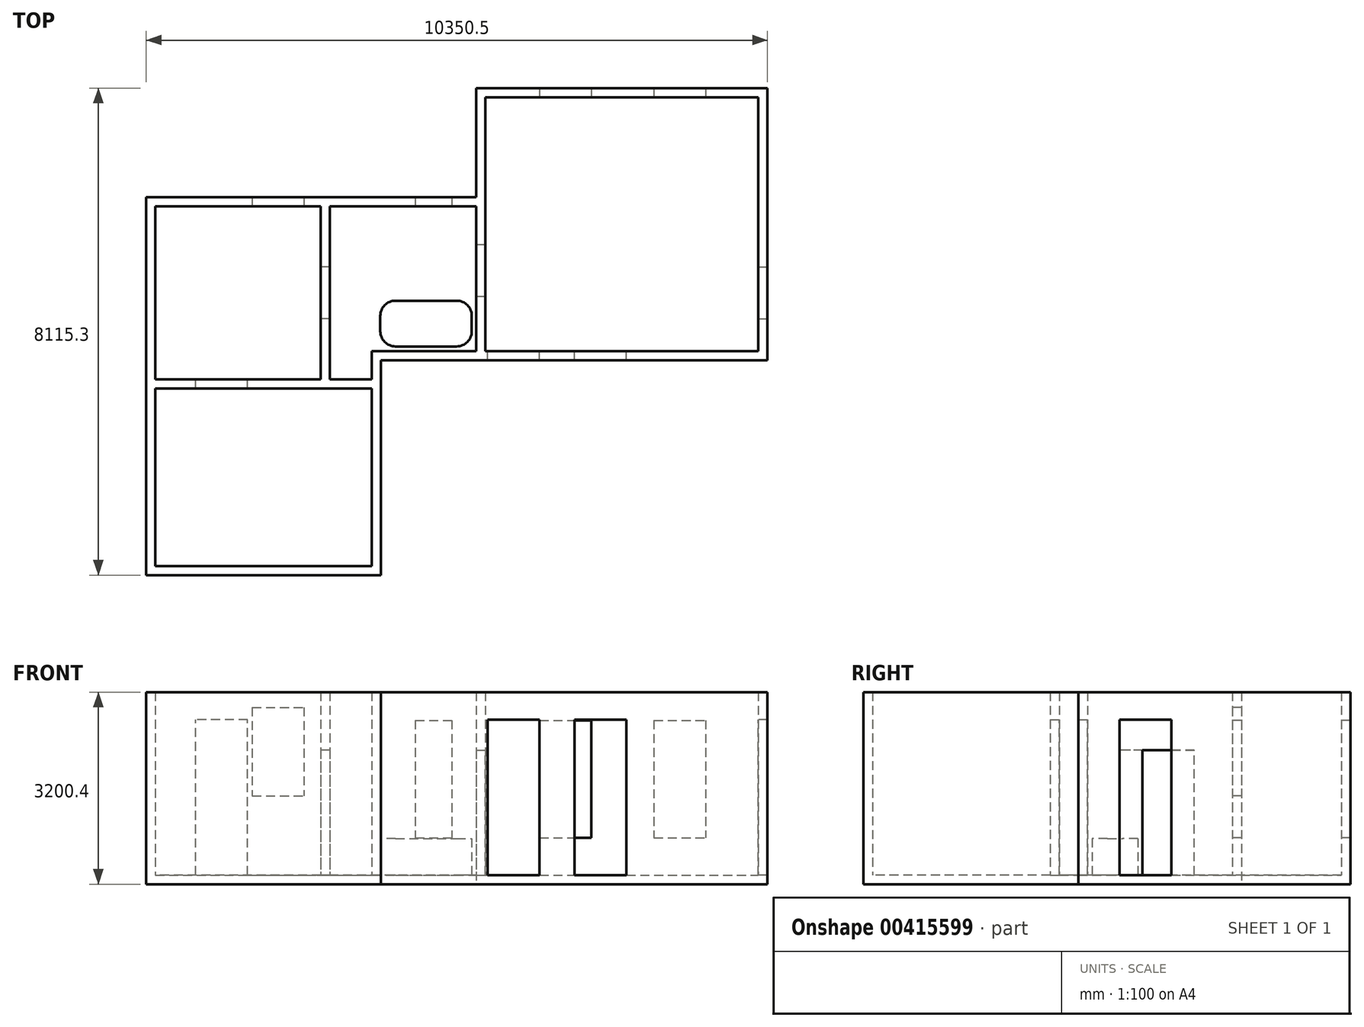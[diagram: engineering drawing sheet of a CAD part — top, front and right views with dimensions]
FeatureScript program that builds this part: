
annotation { "Feature Type Name" : "Feature", "Feature Type Description" : "" }
export const myFeature = defineFeature(function(context is Context, id is Id, definition is map)
    precondition{}
    {
        {
            var Q0;
            Q0=qCreatedBy(makeId("Top.planeOp"),FACE);
            var sketch = newSketch(context, id + "F0", { "sketchPlane" : qUnion([Q0])});
            skLineSegment(sketch, "E0", {"start": v(0, 0) * mm, "end": v(-4546.6, 0) * mm});
            skLineSegment(sketch, "E1", {"start": v(-10045.7, -1816.1) * mm, "end": v(-10045.7, -7810.5) * mm});
            skLineSegment(sketch, "E2", {"start": v(-10045.7, -7810.5) * mm, "end": v(-6438.9, -7810.5) * mm});
            skLineSegment(sketch, "E3", {"start": v(-6438.9, -7810.5) * mm, "end": v(-6438.9, -4229.1) * mm});
            skLineSegment(sketch, "E4", {"start": v(-6438.9, -4229.1) * mm, "end": v(0, -4229.1) * mm});
            skLineSegment(sketch, "E5", {"start": v(0, -4229.1) * mm, "end": v(0, 0) * mm});
            skLineSegment(sketch, "E6", {"start": v(-4546.6, 0) * mm, "end": v(-4546.6, -1816.1) * mm});
            skLineSegment(sketch, "E7", {"start": v(-4546.6, -1816.1) * mm, "end": v(-10045.7, -1816.1) * mm});
            skLineSegment(sketch, "E8.0", {"start": v(-4699, 152.4) * mm, "end": v(-4699, -1663.7) * mm});
            skLineSegment(sketch, "E8.1", {"start": v(152.4, 152.4) * mm, "end": v(-4699, 152.4) * mm});
            skLineSegment(sketch, "E8.2", {"start": v(-4699, -1663.7) * mm, "end": v(-10198.1, -1663.7) * mm});
            skLineSegment(sketch, "E8.3", {"start": v(152.4, -4381.5) * mm, "end": v(152.4, 152.4) * mm});
            skLineSegment(sketch, "E8.4", {"start": v(-10198.1, -1663.7) * mm, "end": v(-10198.1, -7962.9) * mm});
            skLineSegment(sketch, "E8.5", {"start": v(-10198.1, -7962.9) * mm, "end": v(-6286.5, -7962.9) * mm});
            skLineSegment(sketch, "E8.6", {"start": v(-6286.5, -7962.9) * mm, "end": v(-6286.5, -4381.5) * mm});
            skLineSegment(sketch, "E8.7", {"start": v(-6286.5, -4381.5) * mm, "end": v(152.4, -4381.5) * mm});
            skSolve(sketch);
        }
        {
            var Q0;
            Q0 = qSketchRegion(id + "F0", true);
            extrude(context, id + "F1", {"entities" : qUnion([Q0]), "depth" : 3048 * mm});
        }
        {
            var Q0;
            Q0=makeQuery(id+"F1.opExtrude","CAP_FACE",FACE,{"disambiguationData":[OSD([sQuery(id+"F0.wireOp",EDGE,"E0"),sQuery(id+"F0.wireOp",EDGE,"E1"),sQuery(id+"F0.wireOp",EDGE,"E2"),sQuery(id+"F0.wireOp",EDGE,"E3"),sQuery(id+"F0.wireOp",EDGE,"E4"),sQuery(id+"F0.wireOp",EDGE,"E5"),sQuery(id+"F0.wireOp",EDGE,"E6"),sQuery(id+"F0.wireOp",EDGE,"E7"),sQuery(id+"F0.wireOp",EDGE,"E8.0"),sQuery(id+"F0.wireOp",EDGE,"E8.1"),sQuery(id+"F0.wireOp",EDGE,"E8.2"),sQuery(id+"F0.wireOp",EDGE,"E8.3"),sQuery(id+"F0.wireOp",EDGE,"E8.4"),sQuery(id+"F0.wireOp",EDGE,"E8.5"),sQuery(id+"F0.wireOp",EDGE,"E8.6"),sQuery(id+"F0.wireOp",EDGE,"E8.7")])],"isStart":true});
            var sketch = newSketch(context, id + "F2", { "sketchPlane" : qUnion([Q0])});
            skLineSegment(sketch, "E9", {"start": v(-10198.1, 7962.9) * mm, "end": v(-6286.5, 7962.9) * mm});
            skLineSegment(sketch, "E10", {"start": v(-6286.5, 7962.9) * mm, "end": v(-6286.5, 4381.5) * mm});
            skLineSegment(sketch, "E11", {"start": v(-6286.5, 4381.5) * mm, "end": v(152.4, 4381.5) * mm});
            skLineSegment(sketch, "E12", {"start": v(152.4, 4381.5) * mm, "end": v(152.4, -152.4) * mm});
            skLineSegment(sketch, "E13", {"start": v(152.4, -152.4) * mm, "end": v(-4699, -152.4) * mm});
            skLineSegment(sketch, "E14", {"start": v(-4699, -152.4) * mm, "end": v(-4699, 1663.7) * mm});
            skLineSegment(sketch, "E15", {"start": v(-4699, 1663.7) * mm, "end": v(-10198.1, 1663.7) * mm});
            skLineSegment(sketch, "E16", {"start": v(-10198.1, 1663.7) * mm, "end": v(-10198.1, 7962.9) * mm});
            skSolve(sketch);
        }
        {
            var Q0;
            Q0 = qSketchRegion(id + "F2", true);
            extrude(context, id + "F3", {"entities" : qUnion([Q0]), "operationType" : NewBodyOperationType.ADD, "depth" : 152.4 * mm});
        }
        {
            var Q0;
            Q0=makeQuery(id+"F1.opExtrude","SWEPT_FACE",FACE,{"disambiguationData":[OSD([sQuery(id+"F0.wireOp",EDGE,"E4")])]});
            var sketch = newSketch(context, id + "F4", { "sketchPlane" : qUnion([Q0])});
            skLineSegment(sketch, "E17.bottom", {"start": v(2197.1, 0) * mm, "end": v(3060.7, 0) * mm});
            skLineSegment(sketch, "E17.top", {"start": v(2197.1, 2590.8) * mm, "end": v(3060.7, 2590.8) * mm});
            skLineSegment(sketch, "E17.left", {"start": v(2197.1, 0) * mm, "end": v(2197.1, 2590.8) * mm});
            skLineSegment(sketch, "E17.right", {"start": v(3060.7, 0) * mm, "end": v(3060.7, 2590.8) * mm});
            skLineSegment(sketch, "E18.bottom", {"start": v(3644.9, 0) * mm, "end": v(4508.5, 0) * mm});
            skLineSegment(sketch, "E18.top", {"start": v(3644.9, 2590.8) * mm, "end": v(4508.5, 2590.8) * mm});
            skLineSegment(sketch, "E18.left", {"start": v(3644.9, 0) * mm, "end": v(3644.9, 2590.8) * mm});
            skLineSegment(sketch, "E18.right", {"start": v(4508.5, 0) * mm, "end": v(4508.5, 2590.8) * mm});
            skSolve(sketch);
        }
        {
            var Q0;
            Q0 = qSketchRegion(id + "F4", true);
            extrude(context, id + "F5", {"entities" : qUnion([Q0]), "operationType" : NewBodyOperationType.REMOVE, "endBound" : BoundingType.THROUGH_ALL, "oppositeDirection" : true, "depth" : 25.4 * mm});
        }
        {
            var Q0;
            Q0=makeQuery(id+"F1.opExtrude","SWEPT_FACE",FACE,{"disambiguationData":[OSD([sQuery(id+"F0.wireOp",EDGE,"E0")])]});
            var sketch = newSketch(context, id + "F6", { "sketchPlane" : qUnion([Q0])});
            skLineSegment(sketch, "E19.bottom", {"start": v(-3644.9, 2578.1) * mm, "end": v(-2781.3, 2578.1) * mm});
            skLineSegment(sketch, "E19.top", {"start": v(-3644.9, 622.3) * mm, "end": v(-2781.3, 622.3) * mm});
            skLineSegment(sketch, "E19.left", {"start": v(-3644.9, 2578.1) * mm, "end": v(-3644.9, 622.3) * mm});
            skLineSegment(sketch, "E19.right", {"start": v(-2781.3, 2578.1) * mm, "end": v(-2781.3, 622.3) * mm});
            skLineSegment(sketch, "E20.bottom", {"start": v(-1739.9, 2578.1) * mm, "end": v(-876.3, 2578.1) * mm});
            skLineSegment(sketch, "E20.top", {"start": v(-1739.9, 622.3) * mm, "end": v(-876.3, 622.3) * mm});
            skLineSegment(sketch, "E20.left", {"start": v(-1739.9, 2578.1) * mm, "end": v(-1739.9, 622.3) * mm});
            skLineSegment(sketch, "E20.right", {"start": v(-876.3, 2578.1) * mm, "end": v(-876.3, 622.3) * mm});
            skSolve(sketch);
        }
        {
            var Q0;
            Q0 = qSketchRegion(id + "F6", true);
            extrude(context, id + "F7", {"entities" : qUnion([Q0]), "operationType" : NewBodyOperationType.REMOVE, "endBound" : BoundingType.THROUGH_ALL, "oppositeDirection" : true, "depth" : 25.4 * mm});
        }
        {
            var Q0;
            Q0=makeQuery(id+"F1.opExtrude","SWEPT_FACE",FACE,{"disambiguationData":[OSD([sQuery(id+"F0.wireOp",EDGE,"E5")])]});
            var sketch = newSketch(context, id + "F8", { "sketchPlane" : qUnion([Q0])});
            skLineSegment(sketch, "E21.bottom", {"start": v(3695.7, 0) * mm, "end": v(2832.1, 0) * mm});
            skLineSegment(sketch, "E21.top", {"start": v(3695.7, 2590.8) * mm, "end": v(2832.1, 2590.8) * mm});
            skLineSegment(sketch, "E21.left", {"start": v(3695.7, 0) * mm, "end": v(3695.7, 2590.8) * mm});
            skLineSegment(sketch, "E21.right", {"start": v(2832.1, 0) * mm, "end": v(2832.1, 2590.8) * mm});
            skSolve(sketch);
        }
        {
            var Q0;
            Q0 = qSketchRegion(id + "F8", true);
            extrude(context, id + "F9", {"entities" : qUnion([Q0]), "operationType" : NewBodyOperationType.REMOVE, "endBound" : BoundingType.THROUGH_ALL, "oppositeDirection" : true, "depth" : 25.4 * mm});
        }
        {
            var Q0;
            Q0=makeQuery(id+"F9.boolean.opBoolean","MERGE",FACE,{"derivedFrom":[makeQuery(id+"F5.boolean.opBoolean","MERGE",FACE,{"derivedFrom":[makeQuery(id+"F3.opExtrude","CAP_FACE",FACE,{"disambiguationData":[OSD([sQuery(id+"F2.wireOp",EDGE,"E9"),sQuery(id+"F2.wireOp",EDGE,"E10"),sQuery(id+"F2.wireOp",EDGE,"E11"),sQuery(id+"F2.wireOp",EDGE,"E12"),sQuery(id+"F2.wireOp",EDGE,"E13"),sQuery(id+"F2.wireOp",EDGE,"E14"),sQuery(id+"F2.wireOp",EDGE,"E15"),sQuery(id+"F2.wireOp",EDGE,"E16")])],"isStart":true}),makeQuery(id+"F5.opExtrude","SWEPT_FACE",FACE,{"disambiguationData":[OSD([sQuery(id+"F4.wireOp",EDGE,"E17.bottom")])]}),makeQuery(id+"F5.opExtrude","SWEPT_FACE",FACE,{"disambiguationData":[OSD([sQuery(id+"F4.wireOp",EDGE,"E18.bottom")])]})]}),makeQuery(id+"F9.opExtrude","SWEPT_FACE",FACE,{"disambiguationData":[OSD([sQuery(id+"F8.wireOp",EDGE,"E21.bottom")])]})]});
            var sketch = newSketch(context, id + "F10", { "sketchPlane" : qUnion([Q0])});
            skLineSegment(sketch, "E22.bottom", {"start": v(-4546.6, -1816.1) * mm, "end": v(-4699, -1816.1) * mm});
            skLineSegment(sketch, "E22.top", {"start": v(-4546.6, -4229.1) * mm, "end": v(-4699, -4229.1) * mm});
            skLineSegment(sketch, "E22.left", {"start": v(-4546.6, -1816.1) * mm, "end": v(-4546.6, -4229.1) * mm});
            skLineSegment(sketch, "E22.right", {"start": v(-4699, -1816.1) * mm, "end": v(-4699, -4229.1) * mm});
            skLineSegment(sketch, "E23.bottom", {"start": v(-10045.7, -4699) * mm, "end": v(-6438.9, -4699) * mm});
            skLineSegment(sketch, "E23.top", {"start": v(-10045.7, -4851.4) * mm, "end": v(-6438.9, -4851.4) * mm});
            skLineSegment(sketch, "E23.left", {"start": v(-10045.7, -4699) * mm, "end": v(-10045.7, -4851.4) * mm});
            skLineSegment(sketch, "E23.right", {"start": v(-6438.9, -4699) * mm, "end": v(-6438.9, -4851.4) * mm});
            skSolve(sketch);
        }
        {
            var Q0;
            Q0 = qSketchRegion(id + "F10", true);
            var Q1;
            Q1=makeQuery(id+"F1.opExtrude","CAP_FACE",FACE,{"disambiguationData":[OSD([sQuery(id+"F0.wireOp",EDGE,"E0"),sQuery(id+"F0.wireOp",EDGE,"E1"),sQuery(id+"F0.wireOp",EDGE,"E2"),sQuery(id+"F0.wireOp",EDGE,"E3"),sQuery(id+"F0.wireOp",EDGE,"E4"),sQuery(id+"F0.wireOp",EDGE,"E5"),sQuery(id+"F0.wireOp",EDGE,"E6"),sQuery(id+"F0.wireOp",EDGE,"E7"),sQuery(id+"F0.wireOp",EDGE,"E8.0"),sQuery(id+"F0.wireOp",EDGE,"E8.1"),sQuery(id+"F0.wireOp",EDGE,"E8.2"),sQuery(id+"F0.wireOp",EDGE,"E8.3"),sQuery(id+"F0.wireOp",EDGE,"E8.4"),sQuery(id+"F0.wireOp",EDGE,"E8.5"),sQuery(id+"F0.wireOp",EDGE,"E8.6"),sQuery(id+"F0.wireOp",EDGE,"E8.7")])],"isStart":false});
            extrude(context, id + "F11", {"entities" : qUnion([Q0]), "operationType" : NewBodyOperationType.ADD, "endBound" : BoundingType.UP_TO_SURFACE, "endBoundEntityFace" : qUnion([Q1]), "depth" : 25.4 * mm});
        }
        {
            var Q0;
            Q0=makeQuery(id+"F1.opExtrude","SWEPT_FACE",FACE,{"disambiguationData":[OSD([sQuery(id+"F0.wireOp",EDGE,"E7")])]});
            var sketch = newSketch(context, id + "F12", { "sketchPlane" : qUnion([Q0])});
            skLineSegment(sketch, "E24.bottom", {"start": v(-5715, 2578.1) * mm, "end": v(-5105.4, 2578.1) * mm});
            skLineSegment(sketch, "E24.top", {"start": v(-5715, 622.3) * mm, "end": v(-5105.4, 622.3) * mm});
            skLineSegment(sketch, "E24.left", {"start": v(-5715, 2578.1) * mm, "end": v(-5715, 622.3) * mm});
            skLineSegment(sketch, "E24.right", {"start": v(-5105.4, 2578.1) * mm, "end": v(-5105.4, 622.3) * mm});
            skLineSegment(sketch, "E25.bottom", {"start": v(-8432.8, 2794) * mm, "end": v(-7569.2, 2794) * mm});
            skLineSegment(sketch, "E25.top", {"start": v(-8432.8, 1320.8) * mm, "end": v(-7569.2, 1320.8) * mm});
            skLineSegment(sketch, "E25.left", {"start": v(-8432.8, 2794) * mm, "end": v(-8432.8, 1320.8) * mm});
            skLineSegment(sketch, "E25.right", {"start": v(-7569.2, 2794) * mm, "end": v(-7569.2, 1320.8) * mm});
            skSolve(sketch);
        }
        {
            var Q0;
            Q0 = qSketchRegion(id + "F12", true);
            extrude(context, id + "F13", {"entities" : qUnion([Q0]), "operationType" : NewBodyOperationType.REMOVE, "endBound" : BoundingType.THROUGH_ALL, "oppositeDirection" : true, "depth" : 25.4 * mm});
        }
        {
            var Q0;
            Q0=makeQuery(id+"F11.boolean.opBoolean","SPLIT",FACE,{"disambiguationData":[TD([makeQuery(id+"F1.opExtrude","SWEPT_FACE",FACE,{"disambiguationData":[OSD([sQuery(id+"F0.wireOp",EDGE,"E7")])]})])],"derivedFrom":makeQuery(id+"F9.boolean.opBoolean","MERGE",FACE,{"derivedFrom":[makeQuery(id+"F5.boolean.opBoolean","MERGE",FACE,{"derivedFrom":[makeQuery(id+"F3.opExtrude","CAP_FACE",FACE,{"disambiguationData":[OSD([sQuery(id+"F2.wireOp",EDGE,"E9"),sQuery(id+"F2.wireOp",EDGE,"E10"),sQuery(id+"F2.wireOp",EDGE,"E11"),sQuery(id+"F2.wireOp",EDGE,"E12"),sQuery(id+"F2.wireOp",EDGE,"E13"),sQuery(id+"F2.wireOp",EDGE,"E14"),sQuery(id+"F2.wireOp",EDGE,"E15"),sQuery(id+"F2.wireOp",EDGE,"E16")])],"isStart":true}),makeQuery(id+"F5.opExtrude","SWEPT_FACE",FACE,{"disambiguationData":[OSD([sQuery(id+"F4.wireOp",EDGE,"E17.bottom")])]}),makeQuery(id+"F5.opExtrude","SWEPT_FACE",FACE,{"disambiguationData":[OSD([sQuery(id+"F4.wireOp",EDGE,"E18.bottom")])]})]}),makeQuery(id+"F9.opExtrude","SWEPT_FACE",FACE,{"disambiguationData":[OSD([sQuery(id+"F8.wireOp",EDGE,"E21.bottom")])]})]})});
            var sketch = newSketch(context, id + "F14", { "sketchPlane" : qUnion([Q0])});
            skLineSegment(sketch, "E26.bottom", {"start": v(-7289.8, -1816.1) * mm, "end": v(-7137.4, -1816.1) * mm});
            skLineSegment(sketch, "E26.top", {"start": v(-7289.8, -4699) * mm, "end": v(-7137.4, -4699) * mm});
            skLineSegment(sketch, "E26.left", {"start": v(-7289.8, -1816.1) * mm, "end": v(-7289.8, -4699) * mm});
            skLineSegment(sketch, "E26.right", {"start": v(-7137.4, -1816.1) * mm, "end": v(-7137.4, -4699) * mm});
            skSolve(sketch);
        }
        {
            var Q0;
            Q0 = qSketchRegion(id + "F14", true);
            var Q1;
            {var subQ0=sQuery(id+"F0.wireOp",EDGE,"E8.7");var subQ1=sQuery(id+"F0.wireOp",EDGE,"E8.6");var subQ2=sQuery(id+"F0.wireOp",EDGE,"E8.5");var subQ3=sQuery(id+"F0.wireOp",EDGE,"E8.4");var subQ4=sQuery(id+"F0.wireOp",EDGE,"E8.3");var subQ5=sQuery(id+"F0.wireOp",EDGE,"E8.2");var subQ6=sQuery(id+"F0.wireOp",EDGE,"E8.1");var subQ7=sQuery(id+"F0.wireOp",EDGE,"E8.0");var subQ8=sQuery(id+"F0.wireOp",EDGE,"E7");var subQ9=sQuery(id+"F0.wireOp",EDGE,"E6");var subQ10=sQuery(id+"F0.wireOp",EDGE,"E5");var subQ11=sQuery(id+"F0.wireOp",EDGE,"E4");var subQ12=sQuery(id+"F0.wireOp",EDGE,"E3");var subQ13=sQuery(id+"F0.wireOp",EDGE,"E2");var subQ14=sQuery(id+"F0.wireOp",EDGE,"E1");var subQ15=sQuery(id+"F0.wireOp",EDGE,"E0");Q1=makeQuery(id+"F11.boolean.opBoolean","MERGE",FACE,{"derivedFrom":[makeQuery(id+"F1.opExtrude","CAP_FACE",FACE,{"disambiguationData":[OSD([subQ15,subQ14,subQ13,subQ12,subQ11,subQ10,subQ9,subQ8,subQ7,subQ6,subQ5,subQ4,subQ3,subQ2,subQ1,subQ0])],"isStart":false}),makeQuery(id+"F11.opExtrude","CAP_FACE",FACE,{"disambiguationData":[OSD([subQ15,subQ14,subQ13,subQ12,subQ11,subQ10,subQ9,subQ8,subQ7,subQ6,subQ5,subQ4,subQ3,subQ2,subQ1,subQ0]),ownerDisambiguation([makeQuery(id+"F10.imprint","IMPRINT",EDGE,{"derivedFrom":sQuery(id+"F10.wireOp",EDGE,"E22.bottom")})])],"isStart":false}),makeQuery(id+"F11.opExtrude","CAP_FACE",FACE,{"disambiguationData":[OSD([subQ15,subQ14,subQ13,subQ12,subQ11,subQ10,subQ9,subQ8,subQ7,subQ6,subQ5,subQ4,subQ3,subQ2,subQ1,subQ0]),ownerDisambiguation([makeQuery(id+"F10.imprint","IMPRINT",EDGE,{"derivedFrom":sQuery(id+"F10.wireOp",EDGE,"E23.bottom")})])],"isStart":false})]});}
            extrude(context, id + "F15", {"entities" : qUnion([Q0]), "operationType" : NewBodyOperationType.ADD, "endBound" : BoundingType.UP_TO_SURFACE, "endBoundEntityFace" : qUnion([Q1]), "depth" : 25.4 * mm});
        }
        {
            var Q0;
            Q0=makeQuery(id+"F11.boolean.opBoolean","MERGE",FACE,{"derivedFrom":[makeQuery(id+"F1.opExtrude","SWEPT_FACE",FACE,{"disambiguationData":[OSD([sQuery(id+"F0.wireOp",EDGE,"E6")])]}),makeQuery(id+"F11.opExtrude","SWEPT_FACE",FACE,{"disambiguationData":[OSD([sQuery(id+"F10.wireOp",EDGE,"E22.left")])]})]});
            var sketch = newSketch(context, id + "F16", { "sketchPlane" : qUnion([Q0])});
            skLineSegment(sketch, "E27.bottom", {"start": v(-3314.7, 0) * mm, "end": v(-2451.1, 0) * mm});
            skLineSegment(sketch, "E27.top", {"start": v(-3314.7, 2082.8) * mm, "end": v(-2451.1, 2082.8) * mm});
            skLineSegment(sketch, "E27.left", {"start": v(-3314.7, 0) * mm, "end": v(-3314.7, 2082.8) * mm});
            skLineSegment(sketch, "E27.right", {"start": v(-2451.1, 0) * mm, "end": v(-2451.1, 2082.8) * mm});
            skSolve(sketch);
        }
        {
            var Q0;
            Q0 = qSketchRegion(id + "F16", true);
            var Q1;
            Q1=makeQuery(id+"F11.opExtrude","SWEPT_FACE",FACE,{"disambiguationData":[OSD([sQuery(id+"F10.wireOp",EDGE,"E22.right")])]});
            extrude(context, id + "F17", {"entities" : qUnion([Q0]), "operationType" : NewBodyOperationType.REMOVE, "endBound" : BoundingType.UP_TO_SURFACE, "oppositeDirection" : true, "endBoundEntityFace" : qUnion([Q1]), "depth" : 25.4 * mm});
        }
        {
            var Q0;
            {var subQ14=sQuery(id+"F0.wireOp",EDGE,"E1");var subQ16=sQuery(id+"F10.wireOp",EDGE,"E23.bottom");Q0=makeQuery(id+"F15.boolean.opBoolean","SPLIT",FACE,{"disambiguationData":[TD([makeQuery(id+"F1.opExtrude","SWEPT_FACE",FACE,{"disambiguationData":[OSD([subQ14])]})])],"derivedFrom":makeQuery(id+"F11.opExtrude","SWEPT_FACE",FACE,{"disambiguationData":[OSD([subQ16])]})});}
            var sketch = newSketch(context, id + "F18", { "sketchPlane" : qUnion([Q0])});
            skLineSegment(sketch, "E28.bottom", {"start": v(8509, 0) * mm, "end": v(9372.6, 0) * mm});
            skLineSegment(sketch, "E28.top", {"start": v(8509, 2590.8) * mm, "end": v(9372.6, 2590.8) * mm});
            skLineSegment(sketch, "E28.left", {"start": v(8509, 0) * mm, "end": v(8509, 2590.8) * mm});
            skLineSegment(sketch, "E28.right", {"start": v(9372.6, 0) * mm, "end": v(9372.6, 2590.8) * mm});
            skSolve(sketch);
        }
        {
            var Q0;
            Q0 = qSketchRegion(id + "F18", true);
            var Q1;
            Q1=makeQuery(id+"F11.opExtrude","SWEPT_FACE",FACE,{"disambiguationData":[OSD([sQuery(id+"F10.wireOp",EDGE,"E23.top")])]});
            extrude(context, id + "F19", {"entities" : qUnion([Q0]), "operationType" : NewBodyOperationType.REMOVE, "endBound" : BoundingType.UP_TO_SURFACE, "oppositeDirection" : true, "endBoundEntityFace" : qUnion([Q1]), "depth" : 25.4 * mm});
        }
        {
            var Q0;
            Q0=makeQuery(id+"F15.opExtrude","SWEPT_FACE",FACE,{"disambiguationData":[OSD([sQuery(id+"F14.wireOp",EDGE,"E26.left")])]});
            var sketch = newSketch(context, id + "F20", { "sketchPlane" : qUnion([Q0])});
            skLineSegment(sketch, "E29.bottom", {"start": v(2825.75, 2082.8) * mm, "end": v(3689.35, 2082.8) * mm});
            skLineSegment(sketch, "E29.top", {"start": v(2825.75, 0) * mm, "end": v(3689.35, 0) * mm});
            skLineSegment(sketch, "E29.left", {"start": v(2825.75, 2082.8) * mm, "end": v(2825.75, 0) * mm});
            skLineSegment(sketch, "E29.right", {"start": v(3689.35, 2082.8) * mm, "end": v(3689.35, 0) * mm});
            skSolve(sketch);
        }
        {
            var Q0;
            Q0 = qSketchRegion(id + "F20", true);
            var Q1;
            Q1=makeQuery(id+"F15.opExtrude","SWEPT_FACE",FACE,{"disambiguationData":[OSD([sQuery(id+"F14.wireOp",EDGE,"E26.right")])]});
            extrude(context, id + "F21", {"entities" : qUnion([Q0]), "operationType" : NewBodyOperationType.REMOVE, "endBound" : BoundingType.UP_TO_SURFACE, "oppositeDirection" : true, "endBoundEntityFace" : qUnion([Q1]), "depth" : 25.4 * mm});
        }
        {
            var Q0;
            {var subQ0=makeQuery(id+"F1.opExtrude","SWEPT_FACE",FACE,{"disambiguationData":[OSD([sQuery(id+"F0.wireOp",EDGE,"E1")])]});var subQ1=makeQuery(id+"F1.opExtrude","SWEPT_FACE",FACE,{"disambiguationData":[OSD([sQuery(id+"F0.wireOp",EDGE,"E7")])]});var subQ4=makeQuery(id+"F1.opExtrude","SWEPT_FACE",FACE,{"disambiguationData":[OSD([sQuery(id+"F0.wireOp",EDGE,"E3")])]});var subQ6=sQuery(id+"F2.wireOp",EDGE,"E12");var subQ7=sQuery(id+"F2.wireOp",EDGE,"E11");var subQ8=makeQuery(id+"F9.boolean.opBoolean","MERGE",FACE,{"derivedFrom":[makeQuery(id+"F5.boolean.opBoolean","MERGE",FACE,{"derivedFrom":[makeQuery(id+"F3.opExtrude","CAP_FACE",FACE,{"disambiguationData":[OSD([sQuery(id+"F2.wireOp",EDGE,"E9"),sQuery(id+"F2.wireOp",EDGE,"E10"),subQ7,subQ6,sQuery(id+"F2.wireOp",EDGE,"E13"),sQuery(id+"F2.wireOp",EDGE,"E14"),sQuery(id+"F2.wireOp",EDGE,"E15"),sQuery(id+"F2.wireOp",EDGE,"E16")])],"isStart":true}),makeQuery(id+"F5.opExtrude","SWEPT_FACE",FACE,{"disambiguationData":[OSD([sQuery(id+"F4.wireOp",EDGE,"E17.bottom")])]}),makeQuery(id+"F5.opExtrude","SWEPT_FACE",FACE,{"disambiguationData":[OSD([sQuery(id+"F4.wireOp",EDGE,"E18.bottom")])]})]}),makeQuery(id+"F9.opExtrude","SWEPT_FACE",FACE,{"disambiguationData":[OSD([sQuery(id+"F8.wireOp",EDGE,"E21.bottom")])]})]});var subQ9=makeQuery(id+"F11.boolean.opBoolean","SPLIT",FACE,{"disambiguationData":[TD([subQ1])],"derivedFrom":subQ8});Q0=makeQuery(id+"F21.boolean.opBoolean","MERGE",FACE,{"derivedFrom":[makeQuery(id+"F17.boolean.opBoolean","MERGE",FACE,{"derivedFrom":[makeQuery(id+"F11.boolean.opBoolean","SPLIT",FACE,{"disambiguationData":[TD([makeQuery(id+"F1.opExtrude","SWEPT_FACE",FACE,{"disambiguationData":[OSD([sQuery(id+"F0.wireOp",EDGE,"E0")])]})])],"derivedFrom":subQ8}),makeQuery(id+"F15.boolean.opBoolean","SPLIT",FACE,{"disambiguationData":[TD([subQ4])],"derivedFrom":subQ9}),makeQuery(id+"F17.opExtrude","SWEPT_FACE",FACE,{"disambiguationData":[OSD([sQuery(id+"F16.wireOp",EDGE,"E27.bottom")])]})]}),makeQuery(id+"F19.boolean.opBoolean","MERGE",FACE,{"derivedFrom":[makeQuery(id+"F11.boolean.opBoolean","SPLIT",FACE,{"disambiguationData":[TD([makeQuery(id+"F1.opExtrude","SWEPT_FACE",FACE,{"disambiguationData":[OSD([sQuery(id+"F0.wireOp",EDGE,"E2")])]})])],"derivedFrom":subQ8}),makeQuery(id+"F15.boolean.opBoolean","SPLIT",FACE,{"disambiguationData":[TD([subQ0])],"derivedFrom":subQ9}),makeQuery(id+"F19.opExtrude","SWEPT_FACE",FACE,{"disambiguationData":[OSD([sQuery(id+"F18.wireOp",EDGE,"E28.bottom")])]})]}),makeQuery(id+"F21.opExtrude","SWEPT_FACE",FACE,{"disambiguationData":[OSD([sQuery(id+"F20.wireOp",EDGE,"E29.top")])]})]});}
            var sketch = newSketch(context, id + "F22", { "sketchPlane" : qUnion([Q0])});
            skLineSegment(sketch, "E30.bottom", {"start": v(-6045.2, -4152.9) * mm, "end": v(-5029.2, -4152.9) * mm});
            skLineSegment(sketch, "E30.top", {"start": v(-6045.2, -3390.9) * mm, "end": v(-5029.2, -3390.9) * mm});
            skLineSegment(sketch, "E30.left", {"start": v(-6299.2, -3898.9) * mm, "end": v(-6299.2, -3644.9) * mm});
            skLineSegment(sketch, "E30.right", {"start": v(-4775.2, -3898.9) * mm, "end": v(-4775.2, -3644.9) * mm});
            skPoint(sketch, "E31.visualSharp", {"position": v(-6299.2, -4152.9) * mm});
            skArc(sketch, "E31.filletArc", {"start": v(-6299.2, -3898.9) * mm, "mid": v(-6224.8, -4078.5) * mm, "end": v(-6045.2, -4152.9) * mm});
            skPoint(sketch, "E32.visualSharp", {"position": v(-6299.2, -3390.9) * mm});
            skArc(sketch, "E32.filletArc", {"start": v(-6045.2, -3390.9) * mm, "mid": v(-6224.8, -3465.3) * mm, "end": v(-6299.2, -3644.9) * mm});
            skPoint(sketch, "E33.visualSharp", {"position": v(-4775.2, -3390.9) * mm});
            skArc(sketch, "E33.filletArc", {"start": v(-4775.2, -3644.9) * mm, "mid": v(-4849.6, -3465.3) * mm, "end": v(-5029.2, -3390.9) * mm});
            skPoint(sketch, "E34.visualSharp", {"position": v(-4775.2, -4152.9) * mm});
            skArc(sketch, "E34.filletArc", {"start": v(-5029.2, -4152.9) * mm, "mid": v(-4849.6, -4078.5) * mm, "end": v(-4775.2, -3898.9) * mm});
            skSolve(sketch);
        }
        {
            var Q0;
            Q0 = qSketchRegion(id + "F22", true);
            extrude(context, id + "F23", {"entities" : qUnion([Q0]), "operationType" : NewBodyOperationType.ADD, "depth" : 609.6 * mm, "offsetDistance" : 25.4 * mm});
        }
    });
